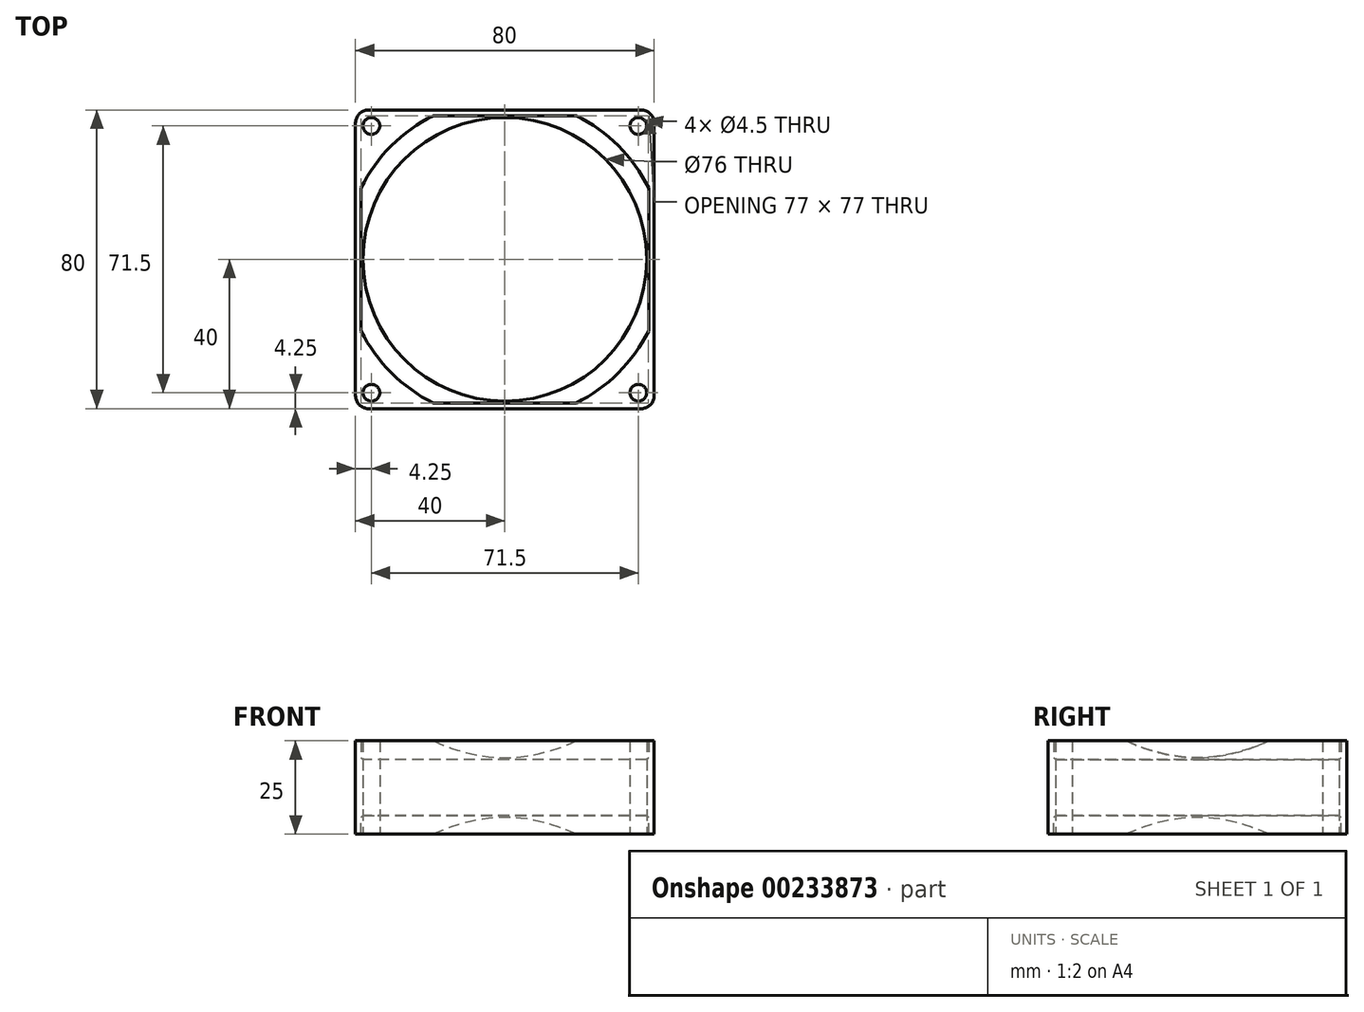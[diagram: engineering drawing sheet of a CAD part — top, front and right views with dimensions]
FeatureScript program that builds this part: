
annotation { "Feature Type Name" : "Feature", "Feature Type Description" : "" }
export const myFeature = defineFeature(function(context is Context, id is Id, definition is map)
    precondition{}
    {
        {
            var Q0;
            Q0=qCreatedBy(makeId("Top.planeOp"),FACE);
            var sketch = newSketch(context, id + "F0", { "sketchPlane" : qUnion([Q0])});
            skLineSegment(sketch, "E0.bottom", {"start": v(36.5, -40) * mm, "end": v(-36.5, -40) * mm});
            skLineSegment(sketch, "E0.top", {"start": v(36.5, 40) * mm, "end": v(-36.5, 40) * mm});
            skLineSegment(sketch, "E0.left", {"start": v(40, -36.5) * mm, "end": v(40, 36.5) * mm});
            skLineSegment(sketch, "E0.right", {"start": v(-40, -36.5) * mm, "end": v(-40, 36.5) * mm});
            skPoint(sketch, "E0.middle", {"position": v(0, 0) * mm});
            skCircle(sketch, "E1", {"center": v(35.75, -35.75) * mm, "radius": 2.25 * mm});
            skCircle(sketch, "E2.0.1.0", {"center": v(35.75, 35.75) * mm, "radius": 2.25 * mm});
            skCircle(sketch, "E2.1.0.0", {"center": v(-35.75, -35.75) * mm, "radius": 2.25 * mm});
            skCircle(sketch, "E2.1.1.0", {"center": v(-35.75, 35.75) * mm, "radius": 2.25 * mm});
            skLineSegment(sketch, "E2.direction2", {"start": v(35.75, -35.75) * mm, "end": v(35.75, 35.75) * mm, "construction": true});
            skLineSegment(sketch, "E3", {"start": v(35.75, 35.75) * mm, "end": v(35.75, 40) * mm, "construction": true});
            skLineSegment(sketch, "E4", {"start": v(35.75, 35.75) * mm, "end": v(40, 35.75) * mm, "construction": true});
            skLineSegment(sketch, "E5", {"start": v(-35.75, 35.75) * mm, "end": v(-40, 35.75) * mm, "construction": true});
            skLineSegment(sketch, "E6", {"start": v(35.75, -35.75) * mm, "end": v(35.75, -40) * mm, "construction": true});
            skCircle(sketch, "E7", {"center": v(0, 0) * mm, "radius": 38 * mm});
            skPoint(sketch, "E8.visualSharp", {"position": v(-40, 40) * mm});
            skArc(sketch, "E8.filletArc", {"start": v(-36.5, 40) * mm, "mid": v(-38.97, 38.97) * mm, "end": v(-40, 36.5) * mm});
            skPoint(sketch, "E9.visualSharp", {"position": v(40, 40) * mm});
            skArc(sketch, "E9.filletArc", {"start": v(40, 36.5) * mm, "mid": v(38.97, 38.97) * mm, "end": v(36.5, 40) * mm});
            skPoint(sketch, "E10.visualSharp", {"position": v(40, -40) * mm});
            skArc(sketch, "E10.filletArc", {"start": v(36.5, -40) * mm, "mid": v(38.97, -38.97) * mm, "end": v(40, -36.5) * mm});
            skPoint(sketch, "E11.visualSharp", {"position": v(-40, -40) * mm});
            skArc(sketch, "E11.filletArc", {"start": v(-40, -36.5) * mm, "mid": v(-38.97, -38.97) * mm, "end": v(-36.5, -40) * mm});
            skSolve(sketch);
        }
        {
            var Q0;
            Q0 = qSketchRegion(id + "F0", true);
            extrude(context, id + "F1", {"entities" : qUnion([Q0]), "depth" : 25 * mm});
        }
        {
            var Q0;
            Q0=makeQuery(id+"F1.opExtrude","CAP_EDGE",EDGE,{"disambiguationData":[OSD([sQuery(id+"F0.wireOp",EDGE,"E7")])],"isStart":false});
            var Q1;
            Q1=makeQuery(id+"F1.opExtrude","CAP_EDGE",EDGE,{"disambiguationData":[OSD([sQuery(id+"F0.wireOp",EDGE,"E7")])],"isStart":true});
            chamfer(context, id + "F2", {"entities" : qUnion([Q0, Q1]), "width" : 5 * mm, "tangentPropagation" : true});
        }
        {
            var Q0;
            Q0=makeQuery(id+"F2.opChamfer","SPLIT",FACE,{"disambiguationData":[OD(3.0)],"derivedFrom":makeQuery(id+"F1.opExtrude","CAP_FACE",FACE,{"disambiguationData":[OSD([sQuery(id+"F0.wireOp",EDGE,"E0.bottom"),sQuery(id+"F0.wireOp",EDGE,"E0.top"),sQuery(id+"F0.wireOp",EDGE,"E0.left"),sQuery(id+"F0.wireOp",EDGE,"E0.right"),sQuery(id+"F0.wireOp",EDGE,"E1"),sQuery(id+"F0.wireOp",EDGE,"E2.0.1.0"),sQuery(id+"F0.wireOp",EDGE,"E2.1.0.0"),sQuery(id+"F0.wireOp",EDGE,"E2.1.1.0"),sQuery(id+"F0.wireOp",EDGE,"E7"),sQuery(id+"F0.wireOp",EDGE,"E8.filletArc"),sQuery(id+"F0.wireOp",EDGE,"E9.filletArc"),sQuery(id+"F0.wireOp",EDGE,"E10.filletArc"),sQuery(id+"F0.wireOp",EDGE,"E11.filletArc")])],"isStart":false})});
            var sketch = newSketch(context, id + "F3", { "sketchPlane" : qUnion([Q0])});
            skLineSegment(sketch, "E12.bottom", {"start": v(-40, 19.15) * mm, "end": v(-38.5, 19.15) * mm});
            skLineSegment(sketch, "E12.top", {"start": v(-40, -19.15) * mm, "end": v(-38.5, -19.15) * mm});
            skLineSegment(sketch, "E12.left", {"start": v(-40, 19.15) * mm, "end": v(-40, -19.15) * mm});
            skLineSegment(sketch, "E12.right", {"start": v(-38.5, 19.15) * mm, "end": v(-38.5, -19.15) * mm});
            skLineSegment(sketch, "E13.1.0", {"start": v(-19.15, -40) * mm, "end": v(19.15, -40) * mm});
            skLineSegment(sketch, "E13.1.1", {"start": v(-19.15, -38.5) * mm, "end": v(19.15, -38.5) * mm});
            skLineSegment(sketch, "E13.1.2", {"start": v(-19.15, -40) * mm, "end": v(-19.15, -38.5) * mm});
            skLineSegment(sketch, "E13.1.3", {"start": v(19.15, -40) * mm, "end": v(19.15, -38.5) * mm});
            skLineSegment(sketch, "E13.2.0", {"start": v(40, -19.15) * mm, "end": v(40, 19.15) * mm});
            skLineSegment(sketch, "E13.2.1", {"start": v(38.5, -19.15) * mm, "end": v(38.5, 19.15) * mm});
            skLineSegment(sketch, "E13.2.2", {"start": v(40, -19.15) * mm, "end": v(38.5, -19.15) * mm});
            skLineSegment(sketch, "E13.2.3", {"start": v(40, 19.15) * mm, "end": v(38.5, 19.15) * mm});
            skLineSegment(sketch, "E13.3.0", {"start": v(19.15, 40) * mm, "end": v(-19.15, 40) * mm});
            skLineSegment(sketch, "E13.3.1", {"start": v(19.15, 38.5) * mm, "end": v(-19.15, 38.5) * mm});
            skLineSegment(sketch, "E13.3.2", {"start": v(19.15, 40) * mm, "end": v(19.15, 38.5) * mm});
            skLineSegment(sketch, "E13.3.3", {"start": v(-19.15, 40) * mm, "end": v(-19.15, 38.5) * mm});
            skPoint(sketch, "E13.center", {"position": v(0, 0) * mm});
            skSolve(sketch);
        }
        {
            var Q0;
            Q0 = qSketchRegion(id + "F3", true);
            var Q1;
            Q1=makeQuery(id+"F2.opChamfer","SPLIT",FACE,{"disambiguationData":[OD(3.0)],"derivedFrom":makeQuery(id+"F1.opExtrude","CAP_FACE",FACE,{"disambiguationData":[OSD([sQuery(id+"F0.wireOp",EDGE,"E0.bottom"),sQuery(id+"F0.wireOp",EDGE,"E0.top"),sQuery(id+"F0.wireOp",EDGE,"E0.left"),sQuery(id+"F0.wireOp",EDGE,"E0.right"),sQuery(id+"F0.wireOp",EDGE,"E1"),sQuery(id+"F0.wireOp",EDGE,"E2.0.1.0"),sQuery(id+"F0.wireOp",EDGE,"E2.1.0.0"),sQuery(id+"F0.wireOp",EDGE,"E2.1.1.0"),sQuery(id+"F0.wireOp",EDGE,"E7"),sQuery(id+"F0.wireOp",EDGE,"E8.filletArc"),sQuery(id+"F0.wireOp",EDGE,"E9.filletArc"),sQuery(id+"F0.wireOp",EDGE,"E10.filletArc"),sQuery(id+"F0.wireOp",EDGE,"E11.filletArc")])],"isStart":true})});
            extrude(context, id + "F4", {"entities" : qUnion([Q0]), "operationType" : NewBodyOperationType.ADD, "endBound" : BoundingType.UP_TO_SURFACE, "oppositeDirection" : true, "endBoundEntityFace" : qUnion([Q1]), "depth" : 25 * mm});
        }
    });
